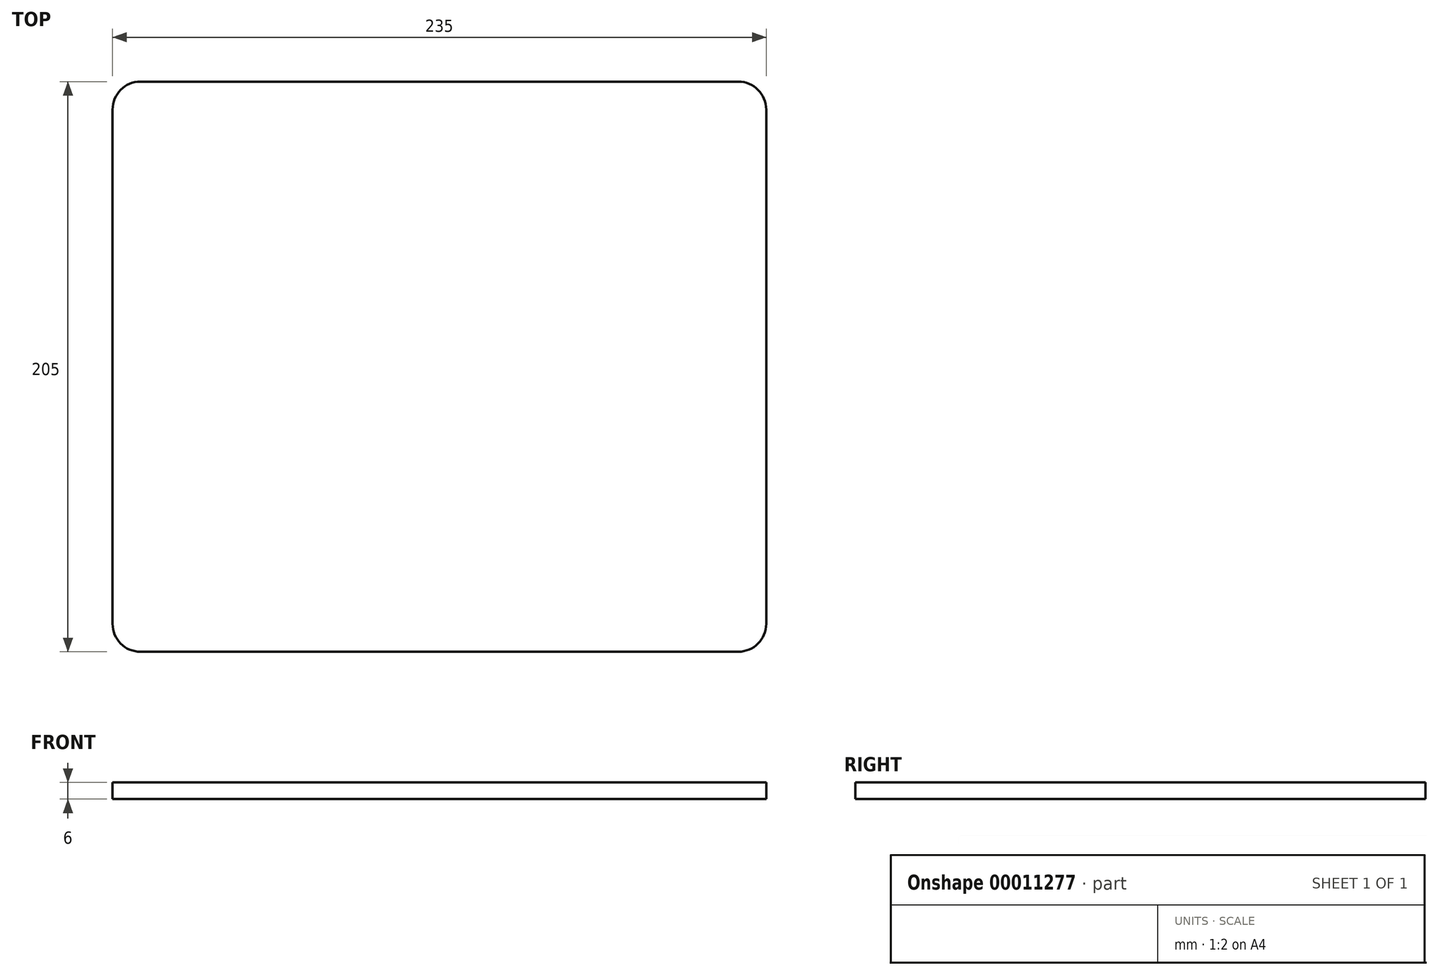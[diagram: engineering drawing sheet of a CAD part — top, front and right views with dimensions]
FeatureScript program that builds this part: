
annotation { "Feature Type Name" : "Feature", "Feature Type Description" : "" }
export const myFeature = defineFeature(function(context is Context, id is Id, definition is map)
    precondition{}
    {
        {
            var Q0;
            Q0=qCreatedBy(makeId("Top.planeOp"),FACE);
            var sketch = newSketch(context, id + "F0", { "sketchPlane" : qUnion([Q0])});
            skLineSegment(sketch, "E0.rect.bottom", {"start": v(107.5, 102.5) * mm, "end": v(-107.5, 102.5) * mm});
            skLineSegment(sketch, "E0.rect.top", {"start": v(107.5, -102.5) * mm, "end": v(-107.5, -102.5) * mm});
            skLineSegment(sketch, "E0.rect.left", {"start": v(117.5, 92.5) * mm, "end": v(117.5, -92.5) * mm});
            skLineSegment(sketch, "E0.rect.right", {"start": v(-117.5, 92.5) * mm, "end": v(-117.5, -92.5) * mm});
            skPoint(sketch, "E0.rect.middle", {"position": v(0, 0) * mm});
            skPoint(sketch, "E1.visualSharp", {"position": v(-117.5, 102.5) * mm});
            skArc(sketch, "E1.filletArc", {"start": v(-107.5, 102.5) * mm, "mid": v(-114.57, 99.57) * mm, "end": v(-117.5, 92.5) * mm});
            skPoint(sketch, "E2.visualSharp", {"position": v(-117.5, -102.5) * mm});
            skArc(sketch, "E2.filletArc", {"start": v(-117.5, -92.5) * mm, "mid": v(-114.57, -99.57) * mm, "end": v(-107.5, -102.5) * mm});
            skPoint(sketch, "E3.visualSharp", {"position": v(117.5, -102.5) * mm});
            skArc(sketch, "E3.filletArc", {"start": v(107.5, -102.5) * mm, "mid": v(114.57, -99.57) * mm, "end": v(117.5, -92.5) * mm});
            skPoint(sketch, "E4.visualSharp", {"position": v(117.5, 102.5) * mm});
            skArc(sketch, "E4.filletArc", {"start": v(117.5, 92.5) * mm, "mid": v(114.57, 99.57) * mm, "end": v(107.5, 102.5) * mm});
            skLineSegment(sketch, "E5", {"start": v(0, 0) * mm, "end": v(0, 102.5) * mm, "construction": true});
            skLineSegment(sketch, "E6.1.0", {"start": v(0, 0) * mm, "end": v(-88.77, 51.25) * mm, "construction": true});
            skLineSegment(sketch, "E6.2.0", {"start": v(0, 0) * mm, "end": v(-88.77, -51.25) * mm, "construction": true});
            skLineSegment(sketch, "E7.1.3.0", {"start": v(0, 0) * mm, "end": v(0, -102.5) * mm, "construction": true});
            skLineSegment(sketch, "E7.1.4.0", {"start": v(0, 0) * mm, "end": v(88.77, -51.25) * mm, "construction": true});
            skLineSegment(sketch, "E7.1.5.0", {"start": v(0, 0) * mm, "end": v(88.77, 51.25) * mm, "construction": true});
            skSolve(sketch);
        }
        {
            var Q0;
            Q0=makeQuery(id+"F0.imprint","IMPRINT",FACE,{"disambiguationData":[TD([[makeQuery(id+"F0.imprint","IMPRINT",EDGE,{"derivedFrom":sQuery(id+"F0.wireOp",EDGE,"E0.rect.bottom")}),1.0]])]});
            extrude(context, id + "F1", {"entities" : qUnion([Q0]), "depth" : 6 * mm});
        }
        {
            var Q0;
            Q0=qCreatedBy(makeId("Front.planeOp"),FACE);
            var sketch = newSketch(context, id + "F2", { "sketchPlane" : qUnion([Q0])});
            skLineSegment(sketch, "E8", {"start": v(0, 0) * mm, "end": v(0, 94.53) * mm, "construction": true});
            skSolve(sketch);
        }
    });
